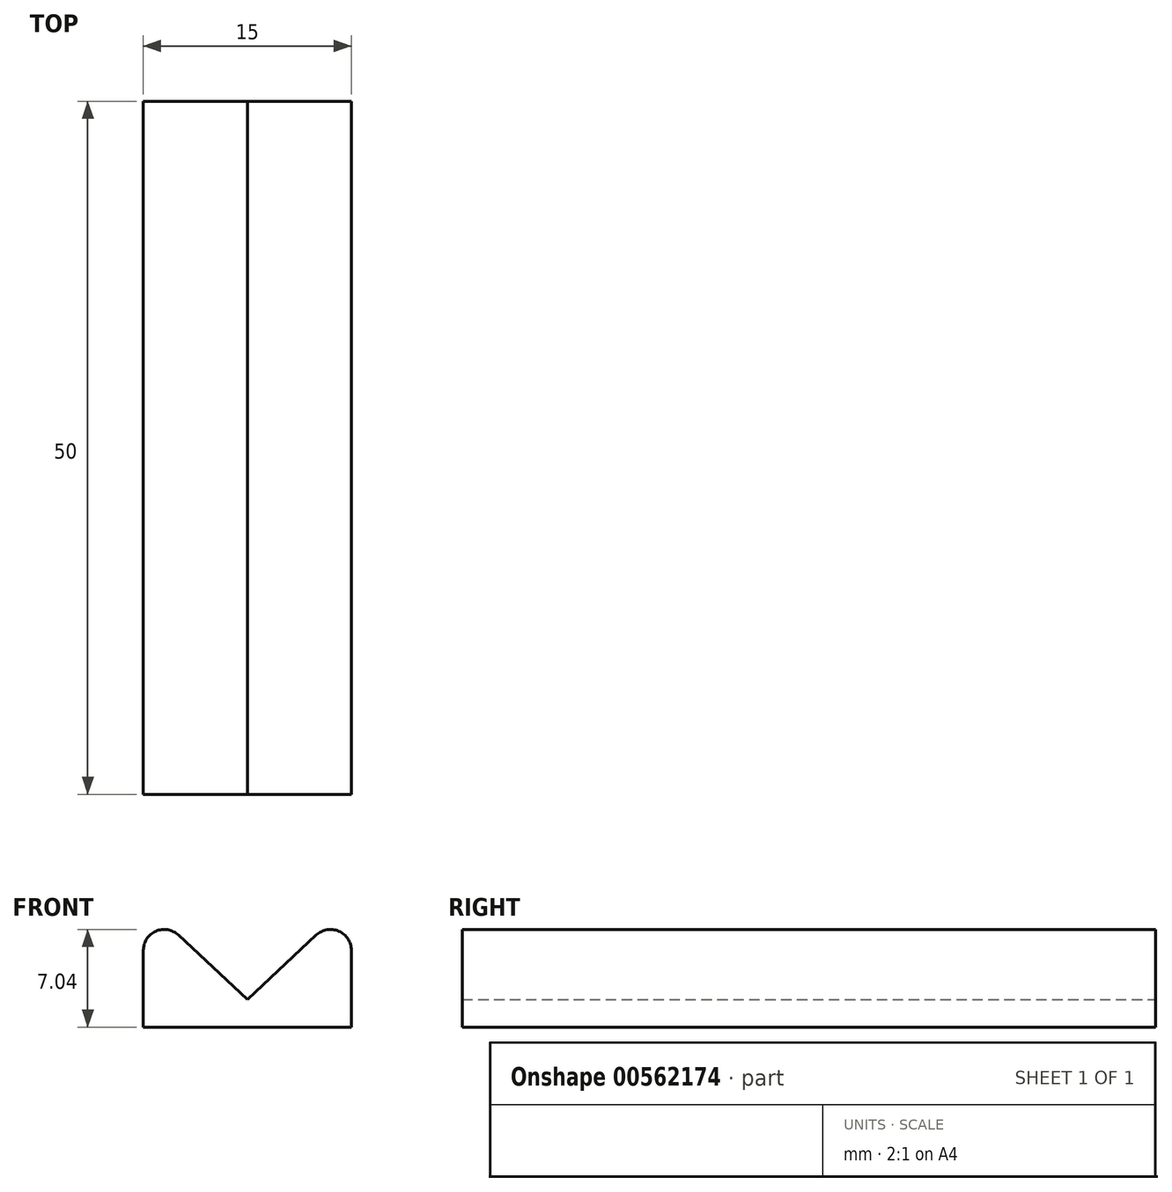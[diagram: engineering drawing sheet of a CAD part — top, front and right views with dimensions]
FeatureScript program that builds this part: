
annotation { "Feature Type Name" : "Feature", "Feature Type Description" : "" }
export const myFeature = defineFeature(function(context is Context, id is Id, definition is map)
    precondition{}
    {
        {
            var Q0;
            Q0=qCreatedBy(makeId("Front.planeOp"),FACE);
            var sketch = newSketch(context, id + "F0", { "sketchPlane" : qUnion([Q0])});
            skLineSegment(sketch, "E0", {"start": v(0, 0) * mm, "end": v(7.5, 0) * mm});
            skLineSegment(sketch, "E1", {"start": v(7.5, 0) * mm, "end": v(7.5, 5.54) * mm});
            skLineSegment(sketch, "E2", {"start": v(4.98, 6.64) * mm, "end": v(0, 2) * mm});
            skPoint(sketch, "E3.visualSharp", {"position": v(7.5, 9) * mm});
            skArc(sketch, "E3.filletArc", {"start": v(7.5, 5.54) * mm, "mid": v(6.6, 6.92) * mm, "end": v(4.98, 6.64) * mm});
            skLineSegment(sketch, "E4.MirrorCS", {"start": v(-4.98, 6.64) * mm, "end": v(0, 2) * mm});
            skArc(sketch, "E5.MirrorCS", {"start": v(-7.5, 5.54) * mm, "mid": v(-6.6, 6.92) * mm, "end": v(-4.98, 6.64) * mm});
            skLineSegment(sketch, "E6.MirrorCS", {"start": v(-7.5, 0) * mm, "end": v(-7.5, 5.54) * mm});
            skLineSegment(sketch, "E7.MirrorCS", {"start": v(0, 0) * mm, "end": v(-7.5, 0) * mm});
            skSolve(sketch);
        }
        {
            var Q0;
            Q0 = qSketchRegion(id + "F0", true);
            extrude(context, id + "F1", {"entities" : qUnion([Q0]), "endBound" : BoundingType.SYMMETRIC, "depth" : 50 * mm, "offsetDistance" : 25 * mm});
        }
    });
